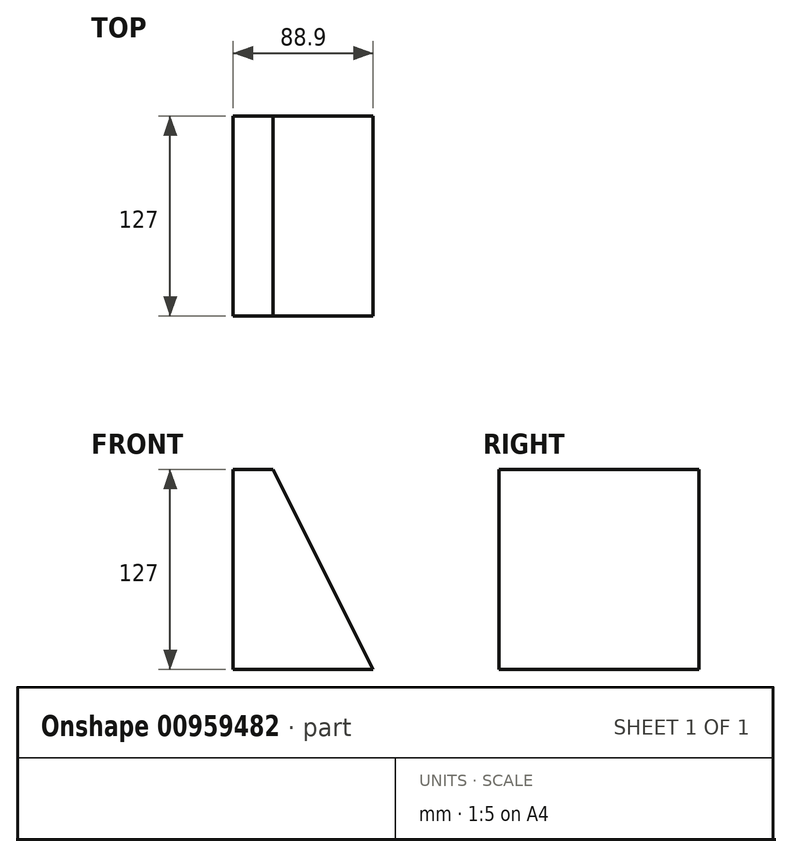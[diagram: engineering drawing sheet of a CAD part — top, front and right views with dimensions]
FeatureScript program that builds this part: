
annotation { "Feature Type Name" : "Feature", "Feature Type Description" : "" }
export const myFeature = defineFeature(function(context is Context, id is Id, definition is map)
    precondition{}
    {
        {
            var Q0;
            Q0=qCreatedBy(makeId("Top.planeOp"),FACE);
            var sketch = newSketch(context, id + "F0", { "sketchPlane" : qUnion([Q0])});
            skLineSegment(sketch, "E0.bottom", {"start": v(-63.5, 63.5) * mm, "end": v(63.5, 63.5) * mm});
            skLineSegment(sketch, "E0.top", {"start": v(-63.5, -63.5) * mm, "end": v(63.5, -63.5) * mm});
            skLineSegment(sketch, "E0.left", {"start": v(-63.5, 63.5) * mm, "end": v(-63.5, -63.5) * mm});
            skLineSegment(sketch, "E0.right", {"start": v(63.5, 63.5) * mm, "end": v(63.5, -63.5) * mm});
            skPoint(sketch, "E0.middle", {"position": v(0, 0) * mm});
            skSolve(sketch);
        }
        {
            var Q0;
            Q0=makeQuery(id+"F0.imprint","IMPRINT",FACE,{"disambiguationData":[TD([[makeQuery(id+"F0.imprint","IMPRINT",EDGE,{"derivedFrom":sQuery(id+"F0.wireOp",EDGE,"E0.bottom")}),-1.0]])]});
            extrude(context, id + "F1", {"entities" : qUnion([Q0]), "depth" : 127 * mm, "offsetDistance" : 25.4 * mm});
        }
        {
            var Q0;
            Q0=makeQuery(id+"F1.opExtrude","CAP_FACE",FACE,{"disambiguationData":[OSD([sQuery(id+"F0.wireOp",EDGE,"E0.bottom"),sQuery(id+"F0.wireOp",EDGE,"E0.top"),sQuery(id+"F0.wireOp",EDGE,"E0.left"),sQuery(id+"F0.wireOp",EDGE,"E0.right")])],"isStart":false});
            var sketch = newSketch(context, id + "F2", { "sketchPlane" : qUnion([Q0])});
            skLineSegment(sketch, "E1.bottom", {"start": v(-63.5, -63.5) * mm, "end": v(-38.1, -63.5) * mm});
            skLineSegment(sketch, "E1.top", {"start": v(-63.5, 63.5) * mm, "end": v(-38.1, 63.5) * mm});
            skLineSegment(sketch, "E1.left", {"start": v(-63.5, -63.5) * mm, "end": v(-63.5, 63.5) * mm});
            skLineSegment(sketch, "E1.right", {"start": v(-38.1, -63.5) * mm, "end": v(-38.1, 63.5) * mm});
            skSolve(sketch);
        }
        {
            var Q0;
            Q0=makeQuery(id+"F1.opExtrude","SWEPT_FACE",FACE,{"disambiguationData":[OSD([sQuery(id+"F0.wireOp",EDGE,"E0.top")])]});
            var sketch = newSketch(context, id + "F3", { "sketchPlane" : qUnion([Q0])});
            skLineSegment(sketch, "E2", {"start": v(-38.1, 127) * mm, "end": v(25.4, 0) * mm});
            skSolve(sketch);
        }
        {
            var Q0;
            {var subQ0=sQuery(id+"F3.wireOp",EDGE,"E2");Q0=makeQuery(id+"F3.imprint","IMPRINT",FACE,{"disambiguationData":[TD([[makeQuery(id+"F3.imprint","IMPRINT",EDGE,{"derivedFrom":subQ0}),1.0]])]});}
            extrude(context, id + "F4", {"entities" : qUnion([Q0]), "operationType" : NewBodyOperationType.REMOVE, "oppositeDirection" : true, "depth" : 127 * mm, "offsetDistance" : 25.4 * mm});
        }
    });
